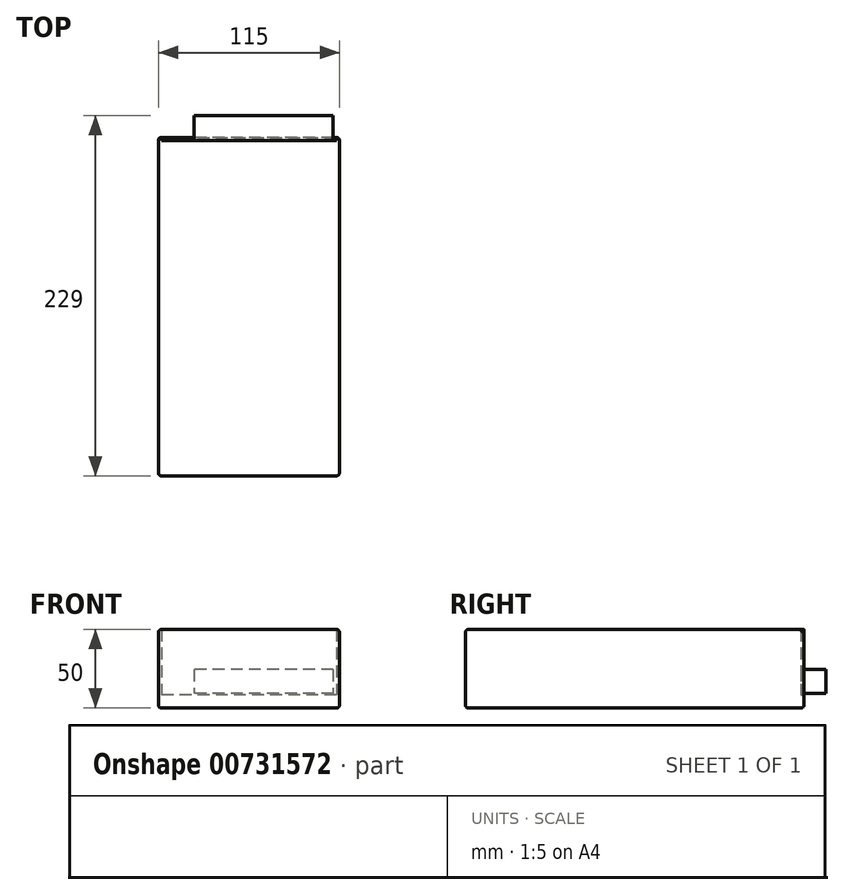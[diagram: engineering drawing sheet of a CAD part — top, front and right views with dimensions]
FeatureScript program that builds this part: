
annotation { "Feature Type Name" : "Feature", "Feature Type Description" : "" }
export const myFeature = defineFeature(function(context is Context, id is Id, definition is map)
    precondition{}
    {
        {
            var Q0;
            Q0=qCreatedBy(makeId("Top.planeOp"),FACE);
            var sketch = newSketch(context, id + "F0", { "sketchPlane" : qUnion([Q0])});
            skLineSegment(sketch, "E0.bottom", {"start": v(-57.5, 107.5) * mm, "end": v(57.5, 107.5) * mm});
            skLineSegment(sketch, "E0.top", {"start": v(-57.5, -107.5) * mm, "end": v(57.5, -107.5) * mm});
            skLineSegment(sketch, "E0.left", {"start": v(-57.5, 107.5) * mm, "end": v(-57.5, -107.5) * mm});
            skLineSegment(sketch, "E0.right", {"start": v(57.5, 107.5) * mm, "end": v(57.5, -107.5) * mm});
            skLineSegment(sketch, "E1", {"start": v(-57.5, 0) * mm, "end": v(0, 0) * mm, "construction": true});
            skLineSegment(sketch, "E2", {"start": v(0, 0) * mm, "end": v(57.5, 0) * mm, "construction": true});
            skLineSegment(sketch, "E3", {"start": v(0, 0) * mm, "end": v(0, 107.5) * mm, "construction": true});
            skLineSegment(sketch, "E4", {"start": v(0, 0) * mm, "end": v(0, -107.5) * mm, "construction": true});
            skSolve(sketch);
        }
        {
            var Q0;
            Q0=makeQuery(id+"F0.imprint","IMPRINT",FACE,{"disambiguationData":[TD([[makeQuery(id+"F0.imprint","IMPRINT",EDGE,{"derivedFrom":sQuery(id+"F0.wireOp",EDGE,"E0.bottom")}),-1.0]])]});
            extrude(context, id + "F1", {"entities" : qUnion([Q0]), "depth" : 50 * mm, "offsetDistance" : 25 * mm, "symmetric" : true});
        }
        {
            var Q0;
            Q0=makeQuery(id+"F1.opExtrude","SWEPT_FACE",FACE,{"disambiguationData":[OSD([sQuery(id+"F0.wireOp",EDGE,"E0.bottom")])]});
            var sketch = newSketch(context, id + "F2", { "sketchPlane" : qUnion([Q0])});
            skLineSegment(sketch, "E5.bottom", {"start": v(-55.5, 25) * mm, "end": v(55.5, 25) * mm});
            skLineSegment(sketch, "E5.top", {"start": v(-55.5, -16.5) * mm, "end": v(55.5, -16.5) * mm});
            skLineSegment(sketch, "E5.left", {"start": v(-55.5, 25) * mm, "end": v(-55.5, -16.5) * mm});
            skLineSegment(sketch, "E5.right", {"start": v(55.5, 25) * mm, "end": v(55.5, -16.5) * mm});
            skSolve(sketch);
        }
        {
            var Q0;
            Q0=makeQuery(id+"F2.imprint","IMPRINT",FACE,{"disambiguationData":[TD([[makeQuery(id+"F2.imprint","IMPRINT",EDGE,{"derivedFrom":sQuery(id+"F2.wireOp",EDGE,"E5.bottom")}),1.0]])]});
            extrude(context, id + "F3", {"entities" : qUnion([Q0]), "operationType" : NewBodyOperationType.REMOVE, "oppositeDirection" : true, "depth" : 2 * mm, "offsetDistance" : 25 * mm});
        }
        {
            var Q0;
            Q0=makeQuery(id+"F3.boolean.opBoolean","COPY",FACE,{"derivedFrom":makeQuery(id+"F3.opExtrude","CAP_FACE",FACE,{"disambiguationData":[OSD([sQuery(id+"F2.wireOp",EDGE,"E5.bottom"),sQuery(id+"F2.wireOp",EDGE,"E5.top"),sQuery(id+"F2.wireOp",EDGE,"E5.left"),sQuery(id+"F2.wireOp",EDGE,"E5.right")])],"isStart":false})});
            var sketch = newSketch(context, id + "F4", { "sketchPlane" : qUnion([Q0])});
            skLineSegment(sketch, "E6.bottom", {"start": v(-53.5, -0.5) * mm, "end": v(35, -0.5) * mm});
            skLineSegment(sketch, "E6.top", {"start": v(-53.5, -15.5) * mm, "end": v(35, -15.5) * mm});
            skLineSegment(sketch, "E6.left", {"start": v(-53.5, -0.5) * mm, "end": v(-53.5, -15.5) * mm});
            skLineSegment(sketch, "E6.right", {"start": v(35, -0.5) * mm, "end": v(35, -15.5) * mm});
            skSolve(sketch);
        }
        {
            var Q0;
            Q0 = qSketchRegion(id + "F4", true);
            extrude(context, id + "F5", {"entities" : qUnion([Q0]), "operationType" : NewBodyOperationType.ADD, "depth" : 16 * mm, "offsetDistance" : 25 * mm});
        }
        {
            var Q0;
            Q0=makeQuery(id+"F1.opExtrude","SWEPT_FACE",FACE,{"disambiguationData":[OSD([sQuery(id+"F0.wireOp",EDGE,"E0.left")])]});
            var Q1;
            Q1=makeQuery(id+"F1.opExtrude","SWEPT_FACE",FACE,{"disambiguationData":[OSD([sQuery(id+"F0.wireOp",EDGE,"E0.right")])]});
            var Q2;
            Q2=makeQuery(id+"F1.opExtrude","CAP_FACE",FACE,{"disambiguationData":[OSD([sQuery(id+"F0.wireOp",EDGE,"E0.bottom"),sQuery(id+"F0.wireOp",EDGE,"E0.top"),sQuery(id+"F0.wireOp",EDGE,"E0.left"),sQuery(id+"F0.wireOp",EDGE,"E0.right")])],"isStart":true});
            var Q3;
            Q3=makeQuery(id+"F1.opExtrude","SWEPT_FACE",FACE,{"disambiguationData":[OSD([sQuery(id+"F0.wireOp",EDGE,"E0.top")])]});
            fillet(context, id + "F6", {"entities" : qUnion([Q0, Q1, Q2, Q3]), "radius" : 2 * mm, "tangentPropagation" : true, "allowEdgeOverflow" : false});
        }
    });
